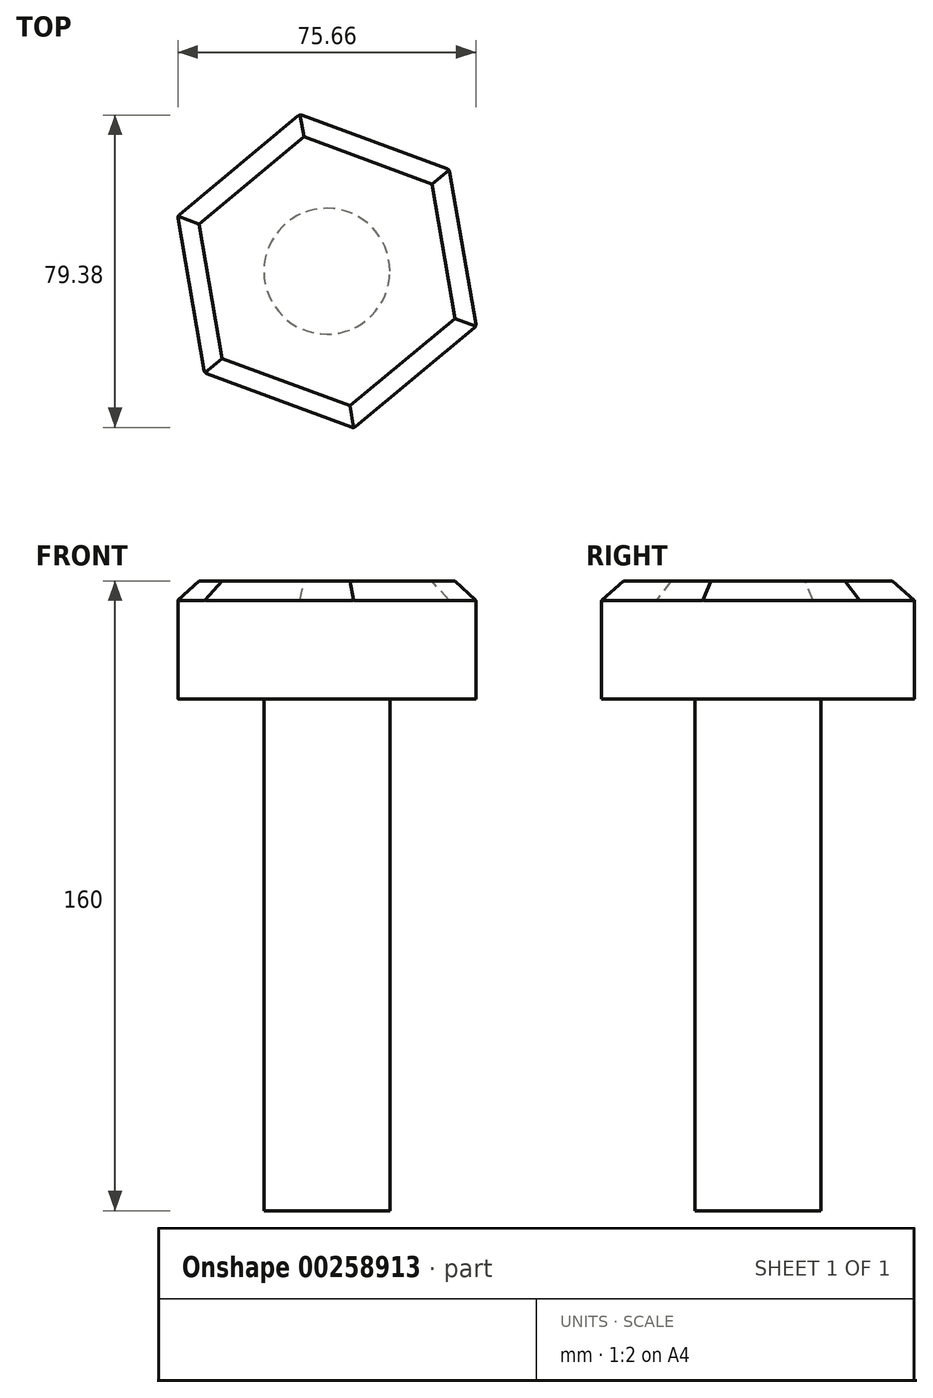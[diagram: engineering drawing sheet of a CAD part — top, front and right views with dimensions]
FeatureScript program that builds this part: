
annotation { "Feature Type Name" : "Feature", "Feature Type Description" : "" }
export const myFeature = defineFeature(function(context is Context, id is Id, definition is map)
    precondition{}
    {
        {
            var Q0;
            Q0=qCreatedBy(makeId("Top.planeOp"),FACE);
            var sketch = newSketch(context, id + "F0", { "sketchPlane" : qUnion([Q0])});
            skCircle(sketch, "E0.cCircle", {"center": v(0, 0) * mm, "radius": 35 * mm, "construction": true});
            skLineSegment(sketch, "E0.0", {"start": v(37.91, -14) * mm, "end": v(6.83, -39.83) * mm});
            skLineSegment(sketch, "E0.1", {"start": v(6.83, -39.83) * mm, "end": v(-31.08, -25.83) * mm});
            skLineSegment(sketch, "E0.2", {"start": v(-31.08, -25.83) * mm, "end": v(-37.91, 14) * mm});
            skLineSegment(sketch, "E0.3", {"start": v(-37.91, 14) * mm, "end": v(-6.83, 39.83) * mm});
            skLineSegment(sketch, "E0.4", {"start": v(-6.83, 39.83) * mm, "end": v(31.08, 25.83) * mm});
            skLineSegment(sketch, "E0.5", {"start": v(31.08, 25.83) * mm, "end": v(37.91, -14) * mm});
            skPoint(sketch, "E0.0.midPoint", {"position": v(22.37, -26.92) * mm});
            skSolve(sketch);
        }
        {
            var Q0;
            Q0=makeQuery(id+"F0.imprint","IMPRINT",FACE,{"disambiguationData":[TD([[makeQuery(id+"F0.imprint","IMPRINT",EDGE,{"derivedFrom":sQuery(id+"F0.wireOp",EDGE,"E0.0")}),-1.0]])]});
            extrude(context, id + "F1", {"entities" : qUnion([Q0]), "depth" : 30 * mm});
        }
        {
            var Q0;
            Q0=makeQuery(id+"F1.opExtrude","CAP_FACE",FACE,{"disambiguationData":[OSD([sQuery(id+"F0.wireOp",EDGE,"E0.0"),sQuery(id+"F0.wireOp",EDGE,"E0.1"),sQuery(id+"F0.wireOp",EDGE,"E0.2"),sQuery(id+"F0.wireOp",EDGE,"E0.3"),sQuery(id+"F0.wireOp",EDGE,"E0.4"),sQuery(id+"F0.wireOp",EDGE,"E0.5")])],"isStart":true});
            var sketch = newSketch(context, id + "F2", { "sketchPlane" : qUnion([Q0])});
            skCircle(sketch, "E1", {"center": v(0, 0) * mm, "radius": 16 * mm});
            skSolve(sketch);
        }
        {
            var Q0;
            Q0=makeQuery(id+"F2.imprint","IMPRINT",FACE,{"disambiguationData":[TD([[makeQuery(id+"F2.imprint","IMPRINT",EDGE,{"derivedFrom":sQuery(id+"F2.wireOp",EDGE,"E1")}),1.0]])]});
            extrude(context, id + "F3", {"entities" : qUnion([Q0]), "operationType" : NewBodyOperationType.ADD, "depth" : 130 * mm});
        }
        {
            var Q0;
            Q0=makeQuery(id+"F1.opExtrude","CAP_EDGE",EDGE,{"disambiguationData":[OSD([sQuery(id+"F0.wireOp",EDGE,"E0.0")])],"isStart":false});
            var Q1;
            Q1=makeQuery(id+"F1.opExtrude","CAP_EDGE",EDGE,{"disambiguationData":[OSD([sQuery(id+"F0.wireOp",EDGE,"E0.1")])],"isStart":false});
            var Q2;
            Q2=makeQuery(id+"F1.opExtrude","CAP_EDGE",EDGE,{"disambiguationData":[OSD([sQuery(id+"F0.wireOp",EDGE,"E0.2")])],"isStart":false});
            var Q3;
            Q3=makeQuery(id+"F1.opExtrude","CAP_EDGE",EDGE,{"disambiguationData":[OSD([sQuery(id+"F0.wireOp",EDGE,"E0.3")])],"isStart":false});
            var Q4;
            Q4=makeQuery(id+"F1.opExtrude","CAP_EDGE",EDGE,{"disambiguationData":[OSD([sQuery(id+"F0.wireOp",EDGE,"E0.4")])],"isStart":false});
            var Q5;
            Q5=makeQuery(id+"F1.opExtrude","CAP_EDGE",EDGE,{"disambiguationData":[OSD([sQuery(id+"F0.wireOp",EDGE,"E0.5")])],"isStart":false});
            chamfer(context, id + "F4", {"entities" : qUnion([Q0, Q1, Q2, Q3, Q4, Q5]), "width" : 5 * mm, "tangentPropagation" : true});
        }
        {
            var Q0;
            Q0=makeQuery(id+"F1.opExtrude","SWEPT_EDGE",EDGE,{"disambiguationData":[OSD([sQuery(id+"F0.wireOp",EDGE,"E0.0"),sQuery(id+"F0.wireOp",EDGE,"E0.1")])]});
            var Q1;
            Q1=makeQuery(id+"F1.opExtrude","SWEPT_EDGE",EDGE,{"disambiguationData":[OSD([sQuery(id+"F0.wireOp",EDGE,"E0.0"),sQuery(id+"F0.wireOp",EDGE,"E0.5")])]});
            var Q2;
            Q2=makeQuery(id+"F1.opExtrude","SWEPT_EDGE",EDGE,{"disambiguationData":[OSD([sQuery(id+"F0.wireOp",EDGE,"E0.4"),sQuery(id+"F0.wireOp",EDGE,"E0.5")])]});
            var Q3;
            Q3=makeQuery(id+"F1.opExtrude","SWEPT_EDGE",EDGE,{"disambiguationData":[OSD([sQuery(id+"F0.wireOp",EDGE,"E0.3"),sQuery(id+"F0.wireOp",EDGE,"E0.4")])]});
            var Q4;
            Q4=makeQuery(id+"F1.opExtrude","SWEPT_EDGE",EDGE,{"disambiguationData":[OSD([sQuery(id+"F0.wireOp",EDGE,"E0.2"),sQuery(id+"F0.wireOp",EDGE,"E0.3")])]});
            var Q5;
            Q5=makeQuery(id+"F1.opExtrude","SWEPT_EDGE",EDGE,{"disambiguationData":[OSD([sQuery(id+"F0.wireOp",EDGE,"E0.1"),sQuery(id+"F0.wireOp",EDGE,"E0.2")])]});
            fillet(context, id + "F5", {"entities" : qUnion([Q0, Q1, Q2, Q3, Q4, Q5]), "radius" : 1 * mm, "tangentPropagation" : true, "allowEdgeOverflow" : false});
        }
    });
